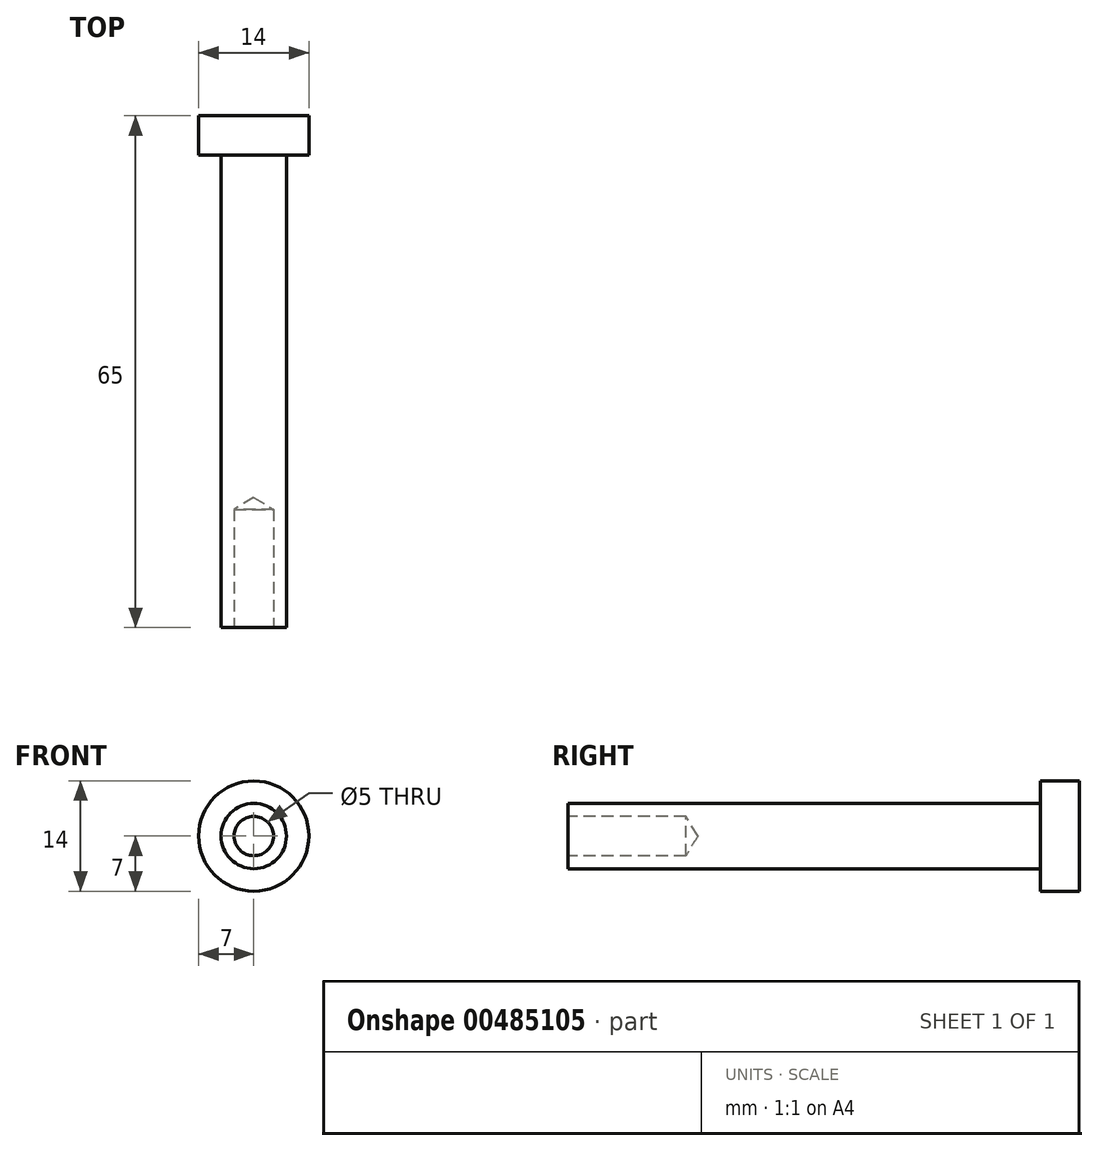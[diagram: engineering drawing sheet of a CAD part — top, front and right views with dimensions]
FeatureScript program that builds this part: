
annotation { "Feature Type Name" : "Feature", "Feature Type Description" : "" }
export const myFeature = defineFeature(function(context is Context, id is Id, definition is map)
    precondition{}
    {
        {
            var Q0;
            Q0=qCreatedBy(makeId("Front.planeOp"),FACE);
            var sketch = newSketch(context, id + "F0", { "sketchPlane" : qUnion([Q0])});
            skCircle(sketch, "E0", {"center": v(0, 0) * mm, "radius": 4.15 * mm});
            skCircle(sketch, "E1", {"center": v(0, 0) * mm, "radius": 7 * mm});
            skSolve(sketch);
        }
        {
            var Q0;
            Q0=makeQuery(id+"F0.imprint","IMPRINT",FACE,{"disambiguationData":[TD([[makeQuery(id+"F0.imprint","IMPRINT",EDGE,{"derivedFrom":sQuery(id+"F0.wireOp",EDGE,"E0")}),1.0]])]});
            extrude(context, id + "F1", {"entities" : qUnion([Q0]), "depth" : 60 * mm});
        }
        {
            var Q0;
            Q0=qSketchRegion(id+"F0",true);
            var Q1;
            Q1=makeQuery(id+"F1.opExtrude","CAP_FACE",FACE,{"disambiguationData":[OSD([sQuery(id+"F0.wireOp",EDGE,"E0")])],"isStart":true});
            extrude(context, id + "F2", {"entities" : qUnion([Q0, Q1]), "operationType" : NewBodyOperationType.ADD, "oppositeDirection" : true, "depth" : 5 * mm});
        }
        {
            var Q0;
            Q0=makeQuery(id+"F1.opExtrude","CAP_FACE",FACE,{"disambiguationData":[OSD([sQuery(id+"F0.wireOp",EDGE,"E0")])],"isStart":false});
            var sketch = newSketch(context, id + "F3", { "sketchPlane" : qUnion([Q0])});
            skCircle(sketch, "E2", {"center": v(0, 0) * mm, "radius": 2.5 * mm});
            skSolve(sketch);
        }
        {
            var Q0;
            Q0=sQuery(id+"F3.wireOp",VERTEX,"E2.center");
            var Q1;
            Q1=makeQuery(id+"F1.opExtrude","SWEPT_BODY",BODY,{"disambiguationData":[OSD([sQuery(id+"F0.wireOp",EDGE,"E0")])]});
            hole(context, id + "F4", {"style" : HoleStyle.SIMPLE, "endStyle" : HoleEndStyle.BLIND, "holeDiameter" : 5 * mm, "holeDepth" : 15 * mm, "isTappedThrough" : true, "tappedDepth" : 12 * mm, "tapClearance" : 3, "locations" : qUnion([Q0]), "scope" : qUnion([Q1])});
        }
    });
